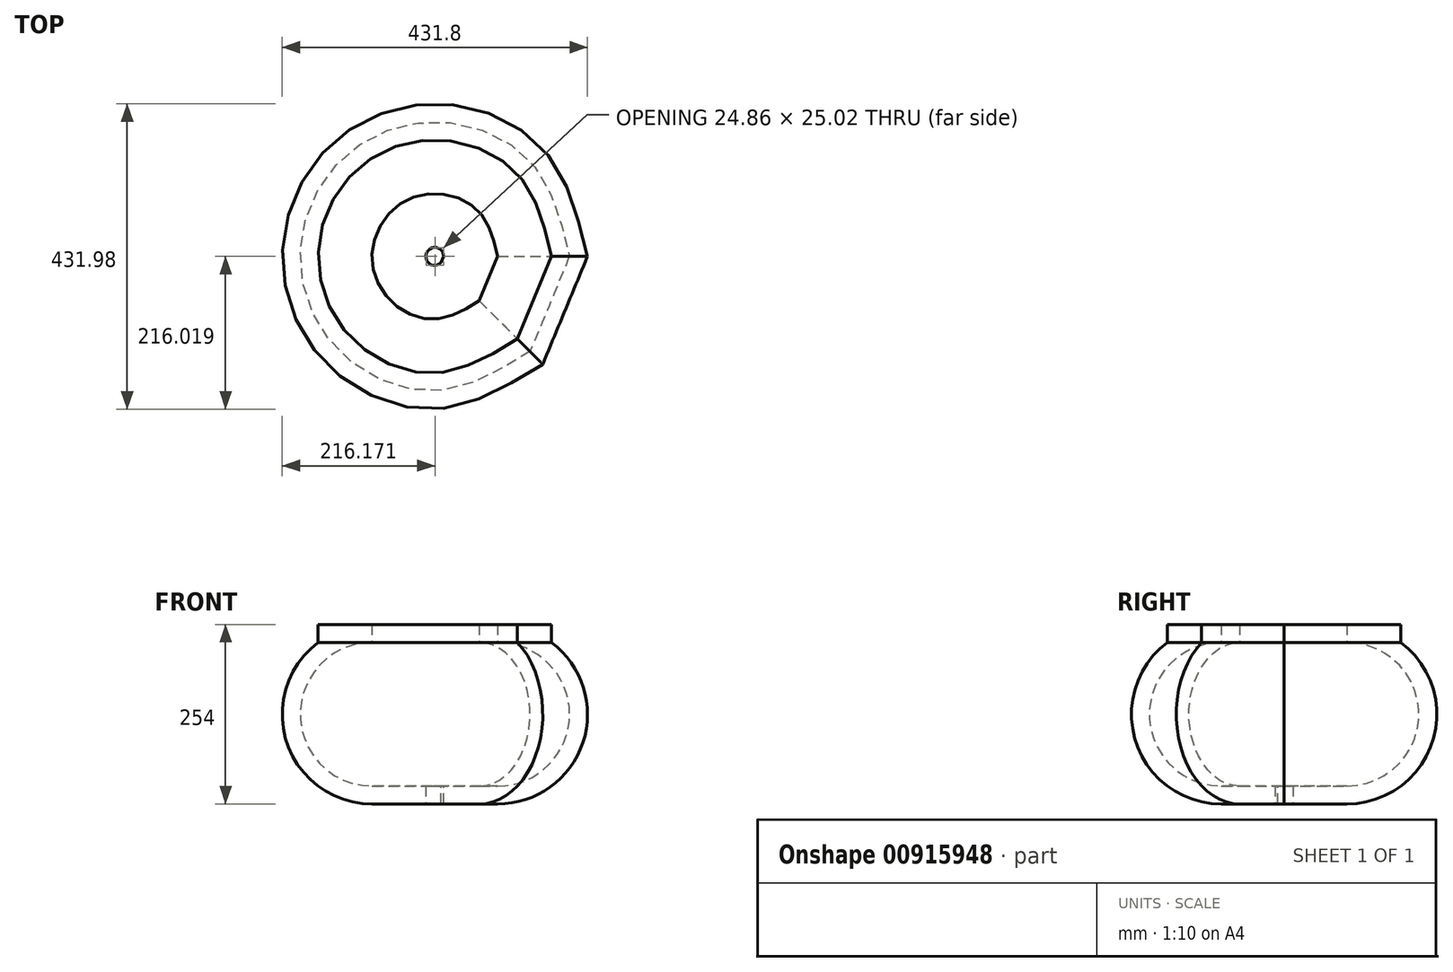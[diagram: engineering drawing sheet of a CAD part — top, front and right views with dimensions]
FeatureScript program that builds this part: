
annotation { "Feature Type Name" : "Feature", "Feature Type Description" : "" }
export const myFeature = defineFeature(function(context is Context, id is Id, definition is map)
    precondition{}
    {
        {
            var Q0;
            Q0=qCreatedBy(makeId("Front.planeOp"),FACE);
            var sketch = newSketch(context, id + "F0", { "sketchPlane" : qUnion([Q0])});
            skArc(sketch, "E0", {"start": v(0, -127) * mm, "mid": v(120.48, -40.16) * mm, "end": v(76.2, 101.6) * mm});
            skArc(sketch, "E1", {"start": v(0, -101.6) * mm, "mid": v(101.6, 0) * mm, "end": v(0, 101.6) * mm});
            skLineSegment(sketch, "E2.bottom", {"start": v(-76.2, -127) * mm, "end": v(0, -127) * mm});
            skLineSegment(sketch, "E2.top", {"start": v(-76.2, -101.6) * mm, "end": v(0, -101.6) * mm});
            skLineSegment(sketch, "E2.left", {"start": v(-76.2, -127) * mm, "end": v(-76.2, -101.6) * mm});
            skLineSegment(sketch, "E3.bottom", {"start": v(0, 127) * mm, "end": v(76.2, 127) * mm});
            skLineSegment(sketch, "E3.left", {"start": v(0, 127) * mm, "end": v(0, 101.6) * mm});
            skLineSegment(sketch, "E3.right", {"start": v(76.2, 127) * mm, "end": v(76.2, 101.6) * mm});
            skLineSegment(sketch, "E4", {"start": v(-88.9, -127) * mm, "end": v(-88.9, 243.86) * mm});
            skSolve(sketch);
        }
        {
            var Q0;
            Q0=sQuery(id+"F0.wireOp",EDGE,"E4");
            cPlane(context, id + "F1", {"entities" : qUnion([Q0]), "cplaneType" : CPlaneType.LINE_ANGLE, "offset" : 25.4 * mm, "angle" : 315 * degree, "width" : 152.4 * mm, "height" : 152.4 * mm});
        }
        {
            var Q0;
            Q0=qCreatedBy(id+"F1.planeOp",FACE);
            var sketch = newSketch(context, id + "F2", { "sketchPlane" : qUnion([Q0])});
            skArc(sketch, "E5", {"start": v(26.04, -127) * mm, "mid": v(146.52, -40.16) * mm, "end": v(102.24, 101.6) * mm});
            skArc(sketch, "E6", {"start": v(26.04, -101.6) * mm, "mid": v(127.64, 0) * mm, "end": v(26.04, 101.6) * mm});
            skLineSegment(sketch, "E7.bottom", {"start": v(-50.16, -127) * mm, "end": v(26.04, -127) * mm});
            skLineSegment(sketch, "E7.top", {"start": v(-50.16, -101.6) * mm, "end": v(26.04, -101.6) * mm});
            skLineSegment(sketch, "E7.left", {"start": v(-50.16, -127) * mm, "end": v(-50.16, -101.6) * mm});
            skLineSegment(sketch, "E8.bottom", {"start": v(26.04, 127) * mm, "end": v(102.24, 127) * mm});
            skLineSegment(sketch, "E8.left", {"start": v(26.04, 127) * mm, "end": v(26.04, 101.6) * mm});
            skLineSegment(sketch, "E8.right", {"start": v(102.24, 127) * mm, "end": v(102.24, 101.6) * mm});
            skLineSegment(sketch, "E9", {"start": v(-62.86, -127) * mm, "end": v(-62.86, 243.86) * mm});
            skSolve(sketch);
        }
        {
            var Q0;
            Q0=sQuery(id+"F2.wireOp",EDGE,"E9");
            cPlane(context, id + "F3", {"entities" : qUnion([Q0]), "cplaneType" : CPlaneType.LINE_ANGLE, "offset" : 25.4 * mm, "angle" : 0 * degree, "width" : 152.4 * mm, "height" : 152.4 * mm});
        }
        {
            var Q0;
            Q0=qCreatedBy(id+"F3.planeOp",FACE);
            var sketch = newSketch(context, id + "F4", { "sketchPlane" : qUnion([Q0])});
            skArc(sketch, "E10", {"start": v(88.9, -127) * mm, "mid": v(209.38, -40.16) * mm, "end": v(165.1, 101.6) * mm});
            skArc(sketch, "E11", {"start": v(88.9, -101.6) * mm, "mid": v(190.5, 0) * mm, "end": v(88.9, 101.6) * mm});
            skLineSegment(sketch, "E12.bottom", {"start": v(12.7, -127) * mm, "end": v(88.9, -127) * mm});
            skLineSegment(sketch, "E12.top", {"start": v(12.7, -101.6) * mm, "end": v(88.9, -101.6) * mm});
            skLineSegment(sketch, "E12.left", {"start": v(12.7, -127) * mm, "end": v(12.7, -101.6) * mm});
            skLineSegment(sketch, "E13.bottom", {"start": v(88.9, 127) * mm, "end": v(165.1, 127) * mm});
            skLineSegment(sketch, "E13.left", {"start": v(88.9, 127) * mm, "end": v(88.9, 101.6) * mm});
            skLineSegment(sketch, "E13.right", {"start": v(165.1, 127) * mm, "end": v(165.1, 101.6) * mm});
            skLineSegment(sketch, "E14", {"start": v(0, -127) * mm, "end": v(0, 297.77) * mm});
            skSolve(sketch);
        }
        {
            var Q0;
            Q0=sQuery(id+"F4.wireOp",EDGE,"E14");
            cPlane(context, id + "F5", {"entities" : qUnion([Q0]), "cplaneType" : CPlaneType.LINE_ANGLE, "offset" : 25.4 * mm, "angle" : 45 * degree, "width" : 152.4 * mm, "height" : 152.4 * mm});
        }
        {
            var Q0;
            Q0=qCreatedBy(id+"F5.planeOp",FACE);
            var sketch = newSketch(context, id + "F6", { "sketchPlane" : qUnion([Q0])});
            skArc(sketch, "E15", {"start": v(151.76, -127) * mm, "mid": v(272.24, -40.16) * mm, "end": v(227.96, 101.6) * mm});
            skArc(sketch, "E16", {"start": v(151.76, -101.6) * mm, "mid": v(253.36, 0) * mm, "end": v(151.76, 101.6) * mm});
            skLineSegment(sketch, "E17.bottom", {"start": v(75.56, -127) * mm, "end": v(151.76, -127) * mm});
            skLineSegment(sketch, "E17.top", {"start": v(75.56, -101.6) * mm, "end": v(151.76, -101.6) * mm});
            skLineSegment(sketch, "E17.left", {"start": v(75.56, -127) * mm, "end": v(75.56, -101.6) * mm});
            skLineSegment(sketch, "E18.bottom", {"start": v(151.76, 127) * mm, "end": v(227.96, 127) * mm});
            skLineSegment(sketch, "E18.left", {"start": v(151.76, 127) * mm, "end": v(151.76, 101.6) * mm});
            skLineSegment(sketch, "E18.right", {"start": v(227.96, 127) * mm, "end": v(227.96, 101.6) * mm});
            skLineSegment(sketch, "E19", {"start": v(62.86, -127) * mm, "end": v(62.86, 297.77) * mm});
            skSolve(sketch);
        }
        {
            var Q0;
            Q0=sQuery(id+"F2.wireOp",EDGE,"E9");
            cPlane(context, id + "F7", {"entities" : qUnion([Q0]), "cplaneType" : CPlaneType.LINE_ANGLE, "offset" : 25.4 * mm, "angle" : 90 * degree, "width" : 152.4 * mm, "height" : 152.4 * mm});
        }
        {
            var Q0;
            Q0=qCreatedBy(id+"F7.planeOp",FACE);
            var sketch = newSketch(context, id + "F8", { "sketchPlane" : qUnion([Q0])});
            skArc(sketch, "E20", {"start": v(177.8, -127) * mm, "mid": v(298.28, -40.16) * mm, "end": v(254, 101.6) * mm});
            skArc(sketch, "E21", {"start": v(177.8, -101.6) * mm, "mid": v(279.4, 0) * mm, "end": v(177.8, 101.6) * mm});
            skLineSegment(sketch, "E22.bottom", {"start": v(101.6, -127) * mm, "end": v(177.8, -127) * mm});
            skLineSegment(sketch, "E22.top", {"start": v(101.6, -101.6) * mm, "end": v(177.8, -101.6) * mm});
            skLineSegment(sketch, "E22.left", {"start": v(101.6, -127) * mm, "end": v(101.6, -101.6) * mm});
            skLineSegment(sketch, "E23.bottom", {"start": v(177.8, 127) * mm, "end": v(254, 127) * mm});
            skLineSegment(sketch, "E23.left", {"start": v(177.8, 127) * mm, "end": v(177.8, 101.6) * mm});
            skLineSegment(sketch, "E23.right", {"start": v(254, 127) * mm, "end": v(254, 101.6) * mm});
            skLineSegment(sketch, "E24", {"start": v(88.9, -127) * mm, "end": v(88.9, 297.77) * mm});
            skSolve(sketch);
        }
        {
            var Q0;
            Q0=sQuery(id+"F2.wireOp",EDGE,"E9");
            cPlane(context, id + "F9", {"entities" : qUnion([Q0]), "cplaneType" : CPlaneType.LINE_ANGLE, "offset" : 25.4 * mm, "angle" : 135 * degree, "oppositeDirection" : true, "width" : 152.4 * mm, "height" : 152.4 * mm});
        }
        {
            var Q0;
            Q0=qCreatedBy(id+"F9.planeOp",FACE);
            var sketch = newSketch(context, id + "F10", { "sketchPlane" : qUnion([Q0])});
            skArc(sketch, "E25", {"start": v(26.04, -127) * mm, "mid": v(146.52, -40.16) * mm, "end": v(102.24, 101.6) * mm});
            skArc(sketch, "E26", {"start": v(26.04, -101.6) * mm, "mid": v(127.64, 0) * mm, "end": v(26.04, 101.6) * mm});
            skLineSegment(sketch, "E27.bottom", {"start": v(-50.16, -127) * mm, "end": v(26.04, -127) * mm});
            skLineSegment(sketch, "E27.top", {"start": v(-50.16, -101.6) * mm, "end": v(26.04, -101.6) * mm});
            skLineSegment(sketch, "E27.left", {"start": v(-50.16, -127) * mm, "end": v(-50.16, -101.6) * mm});
            skLineSegment(sketch, "E28.bottom", {"start": v(26.04, 127) * mm, "end": v(102.24, 127) * mm});
            skLineSegment(sketch, "E28.left", {"start": v(26.04, 127) * mm, "end": v(26.04, 101.6) * mm});
            skLineSegment(sketch, "E28.right", {"start": v(102.24, 127) * mm, "end": v(102.24, 101.6) * mm});
            skLineSegment(sketch, "E29", {"start": v(-62.86, -127) * mm, "end": v(-62.86, 297.77) * mm});
            skSolve(sketch);
        }
        {
            var Q0;
            Q0=sQuery(id+"F8.wireOp",EDGE,"E24");
            cPlane(context, id + "F11", {"entities" : qUnion([Q0]), "cplaneType" : CPlaneType.LINE_ANGLE, "offset" : 25.4 * mm, "angle" : 135 * degree, "width" : 152.4 * mm, "height" : 152.4 * mm});
        }
        {
            var Q0;
            Q0=qCreatedBy(id+"F11.planeOp",FACE);
            var sketch = newSketch(context, id + "F12", { "sketchPlane" : qUnion([Q0])});
            skArc(sketch, "E30", {"start": v(151.76, -127) * mm, "mid": v(272.24, -40.16) * mm, "end": v(227.96, 101.6) * mm});
            skArc(sketch, "E31", {"start": v(151.76, -101.6) * mm, "mid": v(253.36, 0) * mm, "end": v(151.76, 101.6) * mm});
            skLineSegment(sketch, "E32.bottom", {"start": v(75.56, -127) * mm, "end": v(151.76, -127) * mm});
            skLineSegment(sketch, "E32.top", {"start": v(75.56, -101.6) * mm, "end": v(151.76, -101.6) * mm});
            skLineSegment(sketch, "E32.left", {"start": v(75.56, -127) * mm, "end": v(75.56, -101.6) * mm});
            skLineSegment(sketch, "E33.bottom", {"start": v(151.76, 127) * mm, "end": v(227.96, 127) * mm});
            skLineSegment(sketch, "E33.left", {"start": v(151.76, 127) * mm, "end": v(151.76, 101.6) * mm});
            skLineSegment(sketch, "E33.right", {"start": v(227.96, 127) * mm, "end": v(227.96, 101.6) * mm});
            skLineSegment(sketch, "E34", {"start": v(62.86, -127) * mm, "end": v(62.86, 297.77) * mm});
            skSolve(sketch);
        }
        {
            var Q0;
            Q0=sQuery(id+"F2.wireOp",EDGE,"E9");
            cPlane(context, id + "F13", {"entities" : qUnion([Q0]), "cplaneType" : CPlaneType.LINE_ANGLE, "offset" : 25.4 * mm, "angle" : 180 * degree, "width" : 152.4 * mm, "height" : 152.4 * mm});
        }
        {
            var Q0;
            Q0=qCreatedBy(id+"F13.planeOp",FACE);
            var sketch = newSketch(context, id + "F14", { "sketchPlane" : qUnion([Q0])});
            skArc(sketch, "E35", {"start": v(88.9, -127) * mm, "mid": v(209.38, -40.16) * mm, "end": v(165.1, 101.6) * mm});
            skArc(sketch, "E36", {"start": v(88.9, -101.6) * mm, "mid": v(190.5, 0) * mm, "end": v(88.9, 101.6) * mm});
            skLineSegment(sketch, "E37.bottom", {"start": v(12.7, -127) * mm, "end": v(88.9, -127) * mm});
            skLineSegment(sketch, "E37.top", {"start": v(12.7, -101.6) * mm, "end": v(88.9, -101.6) * mm});
            skLineSegment(sketch, "E37.left", {"start": v(12.7, -127) * mm, "end": v(12.7, -101.6) * mm});
            skLineSegment(sketch, "E38.bottom", {"start": v(88.9, 127) * mm, "end": v(165.1, 127) * mm});
            skLineSegment(sketch, "E38.left", {"start": v(88.9, 127) * mm, "end": v(88.9, 101.6) * mm});
            skLineSegment(sketch, "E38.right", {"start": v(165.1, 127) * mm, "end": v(165.1, 101.6) * mm});
            skLineSegment(sketch, "E39", {"start": v(0, -127) * mm, "end": v(0, 348.7) * mm});
            skSolve(sketch);
        }
        {
            var Q0;
            Q0=makeQuery(id+"F0.imprint","IMPRINT",FACE,{"disambiguationData":[TD([[makeQuery(id+"F0.imprint","IMPRINT",EDGE,{"derivedFrom":sQuery(id+"F0.wireOp",EDGE,"E0")}),1.0]])]});
            var Q1;
            Q1=makeQuery(id+"F2.imprint","IMPRINT",FACE,{"disambiguationData":[TD([[makeQuery(id+"F2.imprint","IMPRINT",EDGE,{"derivedFrom":sQuery(id+"F2.wireOp",EDGE,"E5")}),1.0]])]});
            var Q2;
            Q2=makeQuery(id+"F4.imprint","IMPRINT",FACE,{"disambiguationData":[TD([[makeQuery(id+"F4.imprint","IMPRINT",EDGE,{"derivedFrom":sQuery(id+"F4.wireOp",EDGE,"E10")}),1.0]])]});
            var Q3;
            Q3=makeQuery(id+"F6.imprint","IMPRINT",FACE,{"disambiguationData":[TD([[makeQuery(id+"F6.imprint","IMPRINT",EDGE,{"derivedFrom":sQuery(id+"F6.wireOp",EDGE,"E15")}),1.0]])]});
            var Q4;
            Q4=makeQuery(id+"F8.imprint","IMPRINT",FACE,{"disambiguationData":[TD([[makeQuery(id+"F8.imprint","IMPRINT",EDGE,{"derivedFrom":sQuery(id+"F8.wireOp",EDGE,"E20")}),1.0]])]});
            var Q5;
            Q5=makeQuery(id+"F12.imprint","IMPRINT",FACE,{"disambiguationData":[TD([[makeQuery(id+"F12.imprint","IMPRINT",EDGE,{"derivedFrom":sQuery(id+"F12.wireOp",EDGE,"E30")}),1.0]])]});
            var Q6;
            Q6=makeQuery(id+"F14.imprint","IMPRINT",FACE,{"disambiguationData":[TD([[makeQuery(id+"F14.imprint","IMPRINT",EDGE,{"derivedFrom":sQuery(id+"F14.wireOp",EDGE,"E35")}),1.0]])]});
            var Q7;
            Q7=makeQuery(id+"F10.imprint","IMPRINT",FACE,{"disambiguationData":[TD([[makeQuery(id+"F10.imprint","IMPRINT",EDGE,{"derivedFrom":sQuery(id+"F10.wireOp",EDGE,"E25")}),1.0]])]});
            loft(context, id + "F15", {"sheetProfilesArray" : [{ "sheetProfileEntities" : qUnion([Q0]) }, { "sheetProfileEntities" : qUnion([Q1]) }, { "sheetProfileEntities" : qUnion([Q2]) }, { "sheetProfileEntities" : qUnion([Q3]) }, { "sheetProfileEntities" : qUnion([Q4]) }, { "sheetProfileEntities" : qUnion([Q5]) }, { "sheetProfileEntities" : qUnion([Q6]) }, { "sheetProfileEntities" : qUnion([Q7]) }]});
        }
        {
            var Q1;
            Q1=makeQuery(id+"F15.opLoft","CAP_FACE",FACE,{"disambiguationData":[OSD([makeQuery(id+"F10.imprint","IMPRINT",FACE,{"disambiguationData":[TD([[makeQuery(id+"F10.imprint","IMPRINT",EDGE,{"derivedFrom":sQuery(id+"F10.wireOp",EDGE,"E25")}),1.0]])]})])],"isStart":true});
            var Q2;
            Q2=makeQuery(id+"F15.opLoft","CAP_FACE",FACE,{"disambiguationData":[OSD([makeQuery(id+"F0.imprint","IMPRINT",FACE,{"disambiguationData":[TD([[makeQuery(id+"F0.imprint","IMPRINT",EDGE,{"derivedFrom":sQuery(id+"F0.wireOp",EDGE,"E0")}),1.0]])]})])],"isStart":true});
            loft(context, id + "F16", {"operationType" : NewBodyOperationType.ADD, "sheetProfilesArray" : [{ "sheetProfileEntities" : qUnion([Q1]) }, { "sheetProfileEntities" : qUnion([Q2]) }]});
        }
    });
